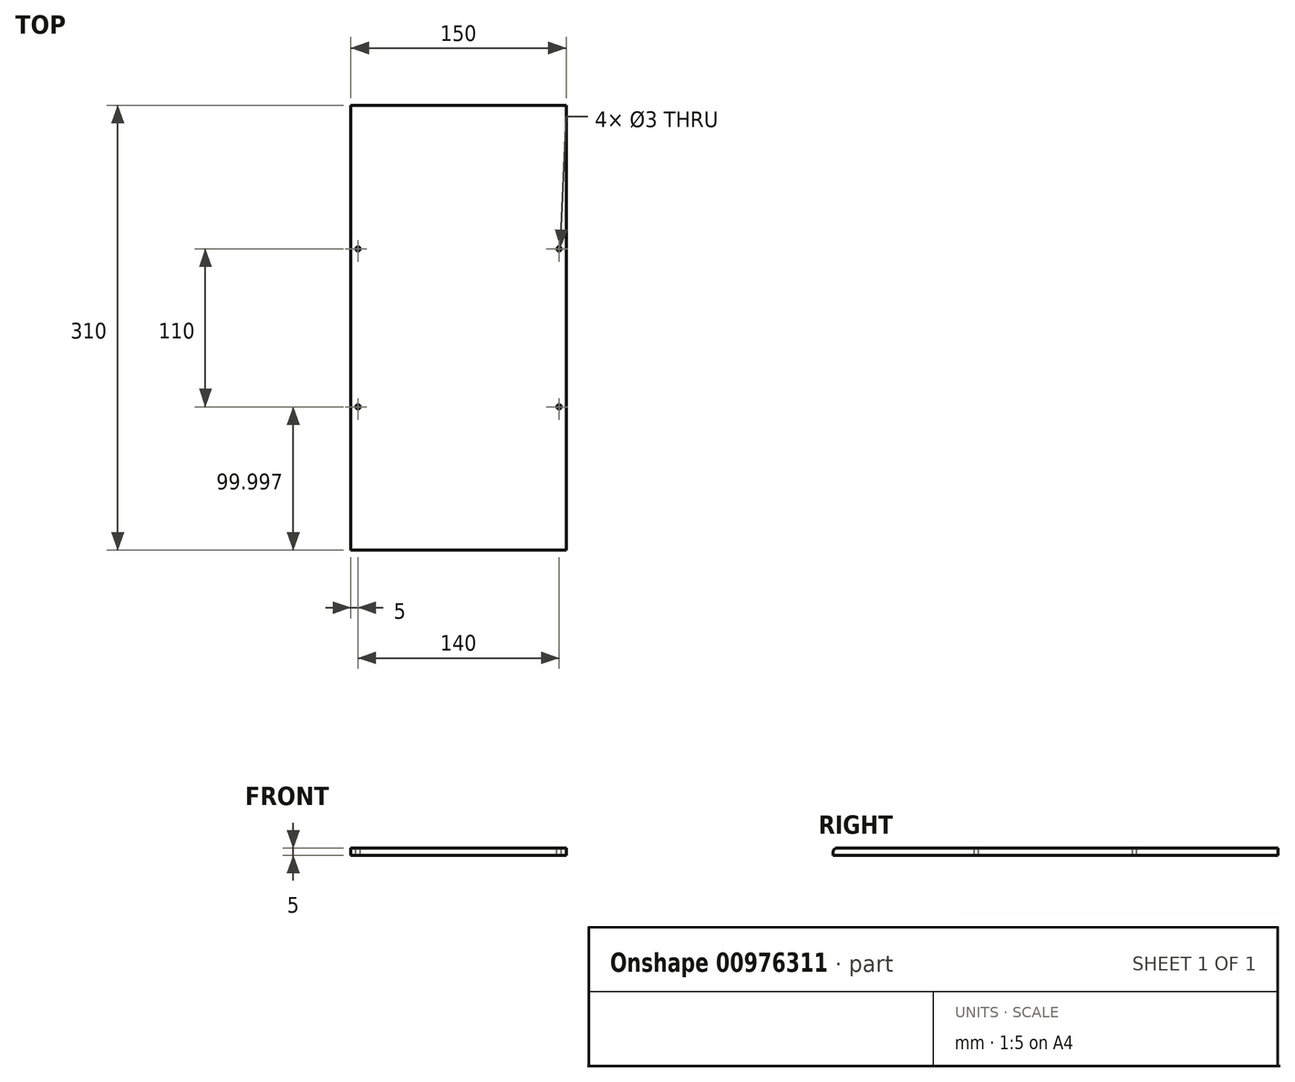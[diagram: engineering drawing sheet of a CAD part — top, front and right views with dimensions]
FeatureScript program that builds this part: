
annotation { "Feature Type Name" : "Feature", "Feature Type Description" : "" }
export const myFeature = defineFeature(function(context is Context, id is Id, definition is map)
    precondition{}
    {
        {
            var Q0;
            Q0=qCreatedBy(makeId("Top.planeOp"),FACE);
            var sketch = newSketch(context, id + "F0", { "sketchPlane" : qUnion([Q0])});
            skLineSegment(sketch, "E0.bottom", {"start": v(-101.7, 168.45) * mm, "end": v(48.3, 168.45) * mm});
            skLineSegment(sketch, "E0.top", {"start": v(-101.7, -141.55) * mm, "end": v(48.3, -141.55) * mm});
            skLineSegment(sketch, "E0.left", {"start": v(-101.7, 168.45) * mm, "end": v(-101.7, -141.55) * mm});
            skLineSegment(sketch, "E0.right", {"start": v(48.3, 168.45) * mm, "end": v(48.3, -141.55) * mm});
            skSolve(sketch);
        }
        {
            var Q0;
            Q0=makeQuery(id+"F0.imprint","IMPRINT",FACE,{"disambiguationData":[TD([[makeQuery(id+"F0.imprint","IMPRINT",EDGE,{"derivedFrom":sQuery(id+"F0.wireOp",EDGE,"E0.bottom")}),-1.0]])]});
            extrude(context, id + "F1", {"entities" : qUnion([Q0]), "depth" : 5 * mm, "offsetDistance" : 25 * mm});
        }
        {
            var Q0;
            Q0=makeQuery(id+"F1.opExtrude","CAP_FACE",FACE,{"disambiguationData":[OSD([sQuery(id+"F0.wireOp",EDGE,"E0.bottom"),sQuery(id+"F0.wireOp",EDGE,"E0.top"),sQuery(id+"F0.wireOp",EDGE,"E0.left"),sQuery(id+"F0.wireOp",EDGE,"E0.right")])],"isStart":false});
            var sketch = newSketch(context, id + "F2", { "sketchPlane" : qUnion([Q0])});
            skCircle(sketch, "E1", {"center": v(-96.7, 68.45) * mm, "radius": 1.5 * mm});
            skCircle(sketch, "E2", {"center": v(-96.7, -41.55) * mm, "radius": 1.5 * mm});
            skCircle(sketch, "E3", {"center": v(43.3, -41.55) * mm, "radius": 1.5 * mm});
            skCircle(sketch, "E4", {"center": v(43.3, 68.45) * mm, "radius": 1.5 * mm});
            skSolve(sketch);
        }
        {
            var Q0;
            Q0 = qSketchRegion(id + "F2", true);
            extrude(context, id + "F3", {"entities" : qUnion([Q0]), "operationType" : NewBodyOperationType.REMOVE, "endBound" : BoundingType.UP_TO_NEXT, "oppositeDirection" : true, "depth" : 25 * mm, "offsetDistance" : 25 * mm});
        }
        {
            var Q0;
            Q0=makeQuery(id+"F1.opExtrude","CAP_EDGE",EDGE,{"disambiguationData":[OSD([sQuery(id+"F0.wireOp",EDGE,"E0.top")])],"isStart":false});
            fillet(context, id + "F4", {"entities" : qUnion([Q0]), "radius" : 3 * mm, "tangentPropagation" : true, "allowEdgeOverflow" : false});
        }
    });
